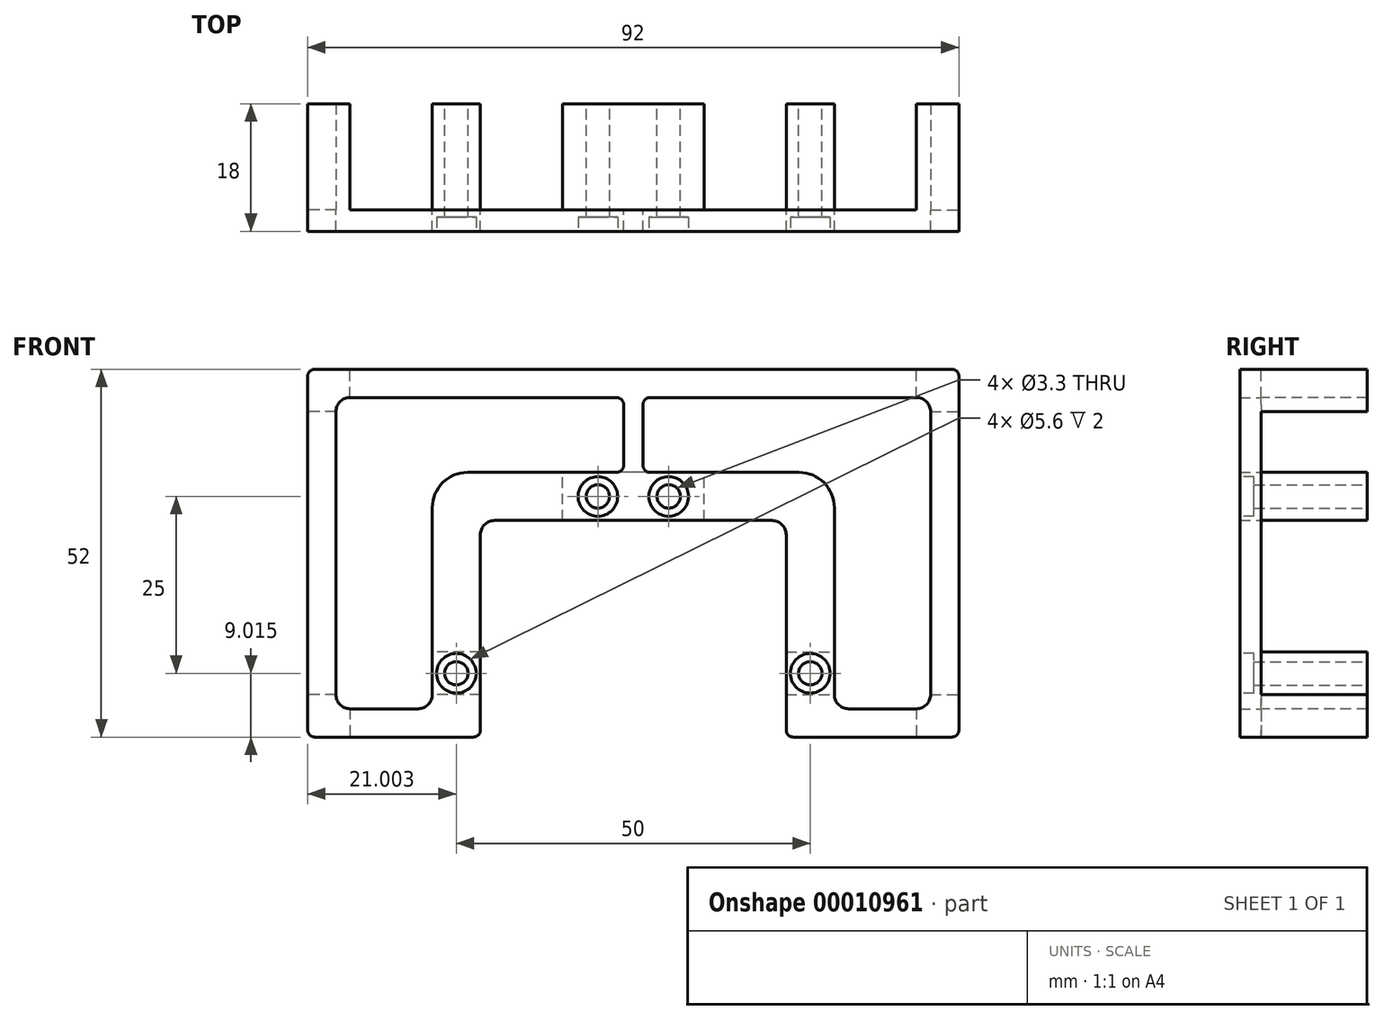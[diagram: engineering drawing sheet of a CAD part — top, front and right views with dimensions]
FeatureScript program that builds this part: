
annotation { "Feature Type Name" : "Feature", "Feature Type Description" : "" }
export const myFeature = defineFeature(function(context is Context, id is Id, definition is map)
    precondition{}
    {
        {
            var Q0;
            Q0=qCreatedBy(makeId("Front.planeOp"),FACE);
            var sketch = newSketch(context, id + "F0", { "sketchPlane" : qUnion([Q0])});
            skCircle(sketch, "E0", {"center": v(12.81, 19.7) * mm, "radius": 1.65 * mm});
            skCircle(sketch, "E1", {"center": v(-7.19, -5.3) * mm, "radius": 1.65 * mm});
            skCircle(sketch, "E2", {"center": v(-7.19, -5.3) * mm, "radius": 2.85 * mm, "construction": true});
            skLineSegment(sketch, "E3", {"start": v(-27.19, 37.68) * mm, "end": v(17.81, 37.68) * mm});
            skLineSegment(sketch, "E4", {"start": v(-28.19, 36.68) * mm, "end": v(-28.19, -13.32) * mm});
            skCircle(sketch, "E5", {"center": v(12.81, 19.7) * mm, "radius": 2.85 * mm, "construction": true});
            skLineSegment(sketch, "E6", {"start": v(12.81, 19.7) * mm, "end": v(-3.79, 19.7) * mm, "construction": true});
            skLineSegment(sketch, "E7", {"start": v(-1.79, 16.3) * mm, "end": v(17.81, 16.3) * mm});
            skLineSegment(sketch, "E8", {"start": v(15.45, 23.1) * mm, "end": v(-5.59, 23.1) * mm});
            skLineSegment(sketch, "E9", {"start": v(12.81, 19.7) * mm, "end": v(12.81, 16.3) * mm, "construction": true});
            skLineSegment(sketch, "E10", {"start": v(12.81, 23.1) * mm, "end": v(12.81, 19.7) * mm, "construction": true});
            skLineSegment(sketch, "E11", {"start": v(17.81, 23.1) * mm, "end": v(17.81, 16.3) * mm});
            skLineSegment(sketch, "E12", {"start": v(-10.59, 18.1) * mm, "end": v(-10.59, -8.32) * mm});
            skLineSegment(sketch, "E13", {"start": v(-3.79, 14.3) * mm, "end": v(-3.79, -13.32) * mm});
            skLineSegment(sketch, "E14", {"start": v(-3.79, -5.3) * mm, "end": v(-7.19, -5.3) * mm, "construction": true});
            skLineSegment(sketch, "E15", {"start": v(-7.19, -5.3) * mm, "end": v(-10.59, -5.3) * mm, "construction": true});
            skLineSegment(sketch, "E16", {"start": v(-4.79, -14.32) * mm, "end": v(-27.19, -14.32) * mm});
            skLineSegment(sketch, "E17", {"start": v(-12.59, -10.32) * mm, "end": v(-22.19, -10.32) * mm});
            skLineSegment(sketch, "E18", {"start": v(-24.19, -8.32) * mm, "end": v(-24.19, 31.68) * mm});
            skLineSegment(sketch, "E19", {"start": v(-22.19, 33.68) * mm, "end": v(15.45, 33.68) * mm});
            skLineSegment(sketch, "E20", {"start": v(17.81, 33.68) * mm, "end": v(17.81, 37.68) * mm});
            skLineSegment(sketch, "E21", {"start": v(-24.19, 33.68) * mm, "end": v(-28.19, 33.68) * mm, "construction": true});
            skPoint(sketch, "E22.visualSharp", {"position": v(-24.19, 33.68) * mm});
            skArc(sketch, "E22.filletArc", {"start": v(-22.19, 33.68) * mm, "mid": v(-23.6, 33.1) * mm, "end": v(-24.19, 31.68) * mm});
            skPoint(sketch, "E23.visualSharp", {"position": v(-24.19, -10.32) * mm});
            skArc(sketch, "E23.filletArc", {"start": v(-24.19, -8.32) * mm, "mid": v(-23.6, -9.74) * mm, "end": v(-22.19, -10.32) * mm});
            skPoint(sketch, "E24.visualSharp", {"position": v(-10.59, -10.32) * mm});
            skArc(sketch, "E24.filletArc", {"start": v(-12.59, -10.32) * mm, "mid": v(-11.17, -9.74) * mm, "end": v(-10.59, -8.32) * mm});
            skLineSegment(sketch, "E25", {"start": v(-17.39, -10.32) * mm, "end": v(-17.39, -14.32) * mm, "construction": true});
            skPoint(sketch, "E26.visualSharp", {"position": v(-10.59, 23.1) * mm});
            skArc(sketch, "E26.filletArc", {"start": v(-5.59, 23.1) * mm, "mid": v(-9.12, 21.63) * mm, "end": v(-10.59, 18.1) * mm});
            skPoint(sketch, "E27.visualSharp", {"position": v(-3.79, 16.3) * mm});
            skArc(sketch, "E27.filletArc", {"start": v(-1.79, 16.3) * mm, "mid": v(-3.2, 15.7) * mm, "end": v(-3.79, 14.3) * mm});
            skPoint(sketch, "E28.visualSharp", {"position": v(-28.19, 37.68) * mm});
            skArc(sketch, "E28.filletArc", {"start": v(-27.19, 37.68) * mm, "mid": v(-27.9, 37.38) * mm, "end": v(-28.19, 36.68) * mm});
            skPoint(sketch, "E29.visualSharp", {"position": v(-28.19, -14.32) * mm});
            skArc(sketch, "E29.filletArc", {"start": v(-28.19, -13.32) * mm, "mid": v(-27.9, -14.03) * mm, "end": v(-27.19, -14.32) * mm});
            skPoint(sketch, "E30.visualSharp", {"position": v(-3.79, -14.32) * mm});
            skArc(sketch, "E30.filletArc", {"start": v(-4.79, -14.32) * mm, "mid": v(-4.08, -14.03) * mm, "end": v(-3.79, -13.32) * mm});
            skLineSegment(sketch, "E31", {"start": v(17.81, 23.1) * mm, "end": v(17.81, 33.68) * mm});
            skLineSegment(sketch, "E32", {"start": v(16.45, 32.68) * mm, "end": v(16.45, 24.1) * mm});
            skArc(sketch, "E33.filletArc", {"start": v(16.45, 32.68) * mm, "mid": v(16.15, 33.38) * mm, "end": v(15.45, 33.68) * mm});
            skPoint(sketch, "E34.newPointB", {"position": v(17.81, 23.1) * mm});
            skArc(sketch, "E34.filletArc", {"start": v(15.45, 23.1) * mm, "mid": v(16.15, 23.39) * mm, "end": v(16.45, 24.1) * mm});
            skSolve(sketch);
        }
        {
            var Q0;
            Q0=makeQuery(id+"F0.imprint","IMPRINT",FACE,{"disambiguationData":[TD([[makeQuery(id+"F0.imprint","IMPRINT",EDGE,{"derivedFrom":sQuery(id+"F0.wireOp",EDGE,"E0")}),-1.0]])]});
            extrude(context, id + "F1", {"entities" : qUnion([Q0]), "depth" : 3 * mm});
        }
        {
            var Q0;
            Q0=makeQuery(id+"F1.opExtrude","CAP_FACE",FACE,{"disambiguationData":[OSD([sQuery(id+"F0.wireOp",EDGE,"E0"),sQuery(id+"F0.wireOp",EDGE,"E1"),sQuery(id+"F0.wireOp",EDGE,"E3"),sQuery(id+"F0.wireOp",EDGE,"E4"),sQuery(id+"F0.wireOp",EDGE,"E7"),sQuery(id+"F0.wireOp",EDGE,"E8"),sQuery(id+"F0.wireOp",EDGE,"E11"),sQuery(id+"F0.wireOp",EDGE,"E12"),sQuery(id+"F0.wireOp",EDGE,"E13"),sQuery(id+"F0.wireOp",EDGE,"E16"),sQuery(id+"F0.wireOp",EDGE,"E17"),sQuery(id+"F0.wireOp",EDGE,"E18"),sQuery(id+"F0.wireOp",EDGE,"E19"),sQuery(id+"F0.wireOp",EDGE,"E20"),sQuery(id+"F0.wireOp",EDGE,"E22.filletArc"),sQuery(id+"F0.wireOp",EDGE,"E23.filletArc"),sQuery(id+"F0.wireOp",EDGE,"E24.filletArc"),sQuery(id+"F0.wireOp",EDGE,"E26.filletArc"),sQuery(id+"F0.wireOp",EDGE,"E27.filletArc")])],"isStart":false});
            var sketch = newSketch(context, id + "F2", { "sketchPlane" : qUnion([Q0])});
            skCircle(sketch, "E35", {"center": v(12.81, 19.7) * mm, "radius": 2.8 * mm});
            skCircle(sketch, "E36", {"center": v(-7.19, -5.3) * mm, "radius": 2.8 * mm});
            skSolve(sketch);
        }
        {
            var Q0;
            Q0=qSketchRegion(id+"F2",true);
            extrude(context, id + "F3", {"entities" : qUnion([Q0]), "operationType" : NewBodyOperationType.REMOVE, "oppositeDirection" : true, "depth" : 2 * mm});
        }
        {
            var Q0;
            Q0=makeQuery(id+"F1.opExtrude","CAP_FACE",FACE,{"disambiguationData":[OSD([sQuery(id+"F0.wireOp",EDGE,"E0"),sQuery(id+"F0.wireOp",EDGE,"E1"),sQuery(id+"F0.wireOp",EDGE,"E3"),sQuery(id+"F0.wireOp",EDGE,"E4"),sQuery(id+"F0.wireOp",EDGE,"E7"),sQuery(id+"F0.wireOp",EDGE,"E8"),sQuery(id+"F0.wireOp",EDGE,"E11"),sQuery(id+"F0.wireOp",EDGE,"E12"),sQuery(id+"F0.wireOp",EDGE,"E13"),sQuery(id+"F0.wireOp",EDGE,"E16"),sQuery(id+"F0.wireOp",EDGE,"E17"),sQuery(id+"F0.wireOp",EDGE,"E18"),sQuery(id+"F0.wireOp",EDGE,"E19"),sQuery(id+"F0.wireOp",EDGE,"E20"),sQuery(id+"F0.wireOp",EDGE,"E22.filletArc"),sQuery(id+"F0.wireOp",EDGE,"E23.filletArc"),sQuery(id+"F0.wireOp",EDGE,"E24.filletArc"),sQuery(id+"F0.wireOp",EDGE,"E26.filletArc"),sQuery(id+"F0.wireOp",EDGE,"E27.filletArc"),sQuery(id+"F0.wireOp",EDGE,"E28.filletArc"),sQuery(id+"F0.wireOp",EDGE,"E29.filletArc"),sQuery(id+"F0.wireOp",EDGE,"E30.filletArc")])],"isStart":true});
            var sketch = newSketch(context, id + "F4", { "sketchPlane" : qUnion([Q0])});
            skCircle(sketch, "E37", {"center": v(-12.81, 19.7) * mm, "radius": 1.65 * mm});
            skCircle(sketch, "E38", {"center": v(7.19, -5.3) * mm, "radius": 1.65 * mm});
            skLineSegment(sketch, "E39.bottom", {"start": v(22.19, 37.68) * mm, "end": v(27.19, 37.68) * mm});
            skLineSegment(sketch, "E39.right", {"start": v(28.19, 36.68) * mm, "end": v(28.19, 31.68) * mm});
            skPoint(sketch, "E40.visualSharp", {"position": v(28.19, 37.68) * mm});
            skArc(sketch, "E40.filletArc", {"start": v(28.19, 36.68) * mm, "mid": v(27.9, 37.38) * mm, "end": v(27.19, 37.68) * mm});
            skPoint(sketch, "E41.visualSharp", {"position": v(24.19, 33.68) * mm});
            skArc(sketch, "E41.filletArc", {"start": v(24.19, 31.68) * mm, "mid": v(23.6, 33.1) * mm, "end": v(22.19, 33.68) * mm});
            skLineSegment(sketch, "E42", {"start": v(24.19, 31.68) * mm, "end": v(28.19, 31.68) * mm});
            skLineSegment(sketch, "E43", {"start": v(22.19, 33.68) * mm, "end": v(22.19, 37.68) * mm});
            skLineSegment(sketch, "E44", {"start": v(28.19, 11.68) * mm, "end": v(18.53, 11.68) * mm, "construction": true});
            skArc(sketch, "E45.MirrorCS", {"start": v(28.19, -13.32) * mm, "mid": v(27.9, -14.03) * mm, "end": v(27.19, -14.32) * mm});
            skArc(sketch, "E46.MirrorCS", {"start": v(24.19, -8.32) * mm, "mid": v(23.6, -9.74) * mm, "end": v(22.19, -10.32) * mm});
            skPoint(sketch, "E47.MirrorP", {"position": v(24.19, -10.32) * mm});
            skPoint(sketch, "E48.MirrorP", {"position": v(28.19, -14.32) * mm});
            skLineSegment(sketch, "E49.MirrorCS", {"start": v(24.19, -8.32) * mm, "end": v(28.19, -8.32) * mm});
            skLineSegment(sketch, "E50.MirrorCS", {"start": v(28.19, -13.32) * mm, "end": v(28.19, -8.32) * mm});
            skLineSegment(sketch, "E51.MirrorCS", {"start": v(22.19, -10.32) * mm, "end": v(22.19, -14.32) * mm});
            skLineSegment(sketch, "E52.MirrorCS", {"start": v(22.19, -14.32) * mm, "end": v(27.19, -14.32) * mm});
            skLineSegment(sketch, "E53.bottom", {"start": v(3.79, -2.29) * mm, "end": v(10.59, -2.29) * mm});
            skLineSegment(sketch, "E53.top", {"start": v(3.79, -8.32) * mm, "end": v(10.59, -8.32) * mm});
            skLineSegment(sketch, "E53.left", {"start": v(3.79, -2.29) * mm, "end": v(3.79, -8.32) * mm});
            skLineSegment(sketch, "E53.right", {"start": v(10.59, -2.29) * mm, "end": v(10.59, -8.32) * mm});
            skLineSegment(sketch, "E54", {"start": v(7.19, -2.29) * mm, "end": v(7.19, -8.32) * mm, "construction": true});
            skLineSegment(sketch, "E55.bottom", {"start": v(-17.81, 16.3) * mm, "end": v(-7.81, 16.3) * mm});
            skLineSegment(sketch, "E55.top", {"start": v(-17.81, 23.1) * mm, "end": v(-7.81, 23.1) * mm});
            skLineSegment(sketch, "E55.left", {"start": v(-17.81, 16.3) * mm, "end": v(-17.81, 23.1) * mm});
            skLineSegment(sketch, "E55.right", {"start": v(-7.81, 16.3) * mm, "end": v(-7.81, 23.1) * mm});
            skLineSegment(sketch, "E56", {"start": v(-7.81, 19.7) * mm, "end": v(-17.81, 19.7) * mm, "construction": true});
            skSolve(sketch);
        }
        {
            var Q0;
            Q0 = qSketchRegion(id + "F4", true);
            extrude(context, id + "F5", {"entities" : qUnion([Q0]), "operationType" : NewBodyOperationType.ADD, "depth" : 15 * mm});
        }
        {
            var Q0;
            Q0=makeQuery(id+"F1.opExtrude","SWEPT_BODY",BODY,{"disambiguationData":[OSD([sQuery(id+"F0.wireOp",EDGE,"E0"),sQuery(id+"F0.wireOp",EDGE,"E1"),sQuery(id+"F0.wireOp",EDGE,"E3"),sQuery(id+"F0.wireOp",EDGE,"E4"),sQuery(id+"F0.wireOp",EDGE,"E7"),sQuery(id+"F0.wireOp",EDGE,"E8"),sQuery(id+"F0.wireOp",EDGE,"E11"),sQuery(id+"F0.wireOp",EDGE,"E12"),sQuery(id+"F0.wireOp",EDGE,"E13"),sQuery(id+"F0.wireOp",EDGE,"E16"),sQuery(id+"F0.wireOp",EDGE,"E17"),sQuery(id+"F0.wireOp",EDGE,"E18"),sQuery(id+"F0.wireOp",EDGE,"E19"),sQuery(id+"F0.wireOp",EDGE,"E20"),sQuery(id+"F0.wireOp",EDGE,"E22.filletArc"),sQuery(id+"F0.wireOp",EDGE,"E23.filletArc"),sQuery(id+"F0.wireOp",EDGE,"E24.filletArc"),sQuery(id+"F0.wireOp",EDGE,"E26.filletArc"),sQuery(id+"F0.wireOp",EDGE,"E27.filletArc"),sQuery(id+"F0.wireOp",EDGE,"E28.filletArc"),sQuery(id+"F0.wireOp",EDGE,"E29.filletArc"),sQuery(id+"F0.wireOp",EDGE,"E30.filletArc")])]});
            var Q1;
            Q1=makeQuery(id+"F1.opExtrude","SWEPT_FACE",FACE,{"disambiguationData":[OSD([sQuery(id+"F0.wireOp",EDGE,"E11")])]});
            mirror(context, id + "F6", {"operationType" : NewBodyOperationType.ADD, "entities" : qUnion([Q0]), "mirrorPlane" : qUnion([Q1])});
        }
    });
